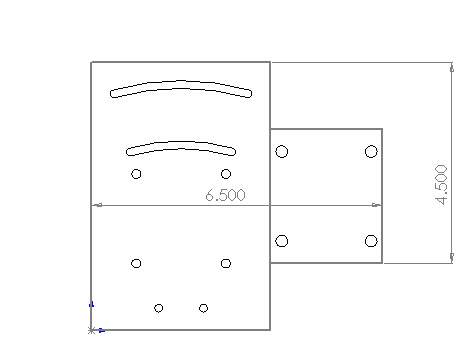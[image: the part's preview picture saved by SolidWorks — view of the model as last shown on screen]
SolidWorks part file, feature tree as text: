
SOLIDWORKS PART (.sldprt)
format: sldprt  version: not decoded by parser v0  size: 266,240 bytes
history: native  units: mm
features: sketch x3, cut_extrude x2, material x1, extrude x1, pattern_linear x1 + 1 further entry (+12 scaffold rows collapsed)
feature tree (21):
  "Annotations"  RD1=165.1mm RD2=114.3mm
  scaffold x12  (default folders/planes/origin — collapsed)
  material  "Material <not specified>"
  sketch  "Sketch1"  dims[c1.D1=152.4mm c1.D2=101.6mm c1.D3=63.5mm c1.D4=63.5mm c2.D3=76.2mm c2.D4=63.5mm c2.D5=38.1mm]
  extrude  "Extrude1"  Depth=12.7mm
  sketch  "Sketch4"  dims[c1.D3=6.6294mm c1.D6=4.3688mm c1.D9=~4.705401mm c1.D10=4.3688mm c2.D6=5.1054mm c2.D1=12.7mm c2.D2=6.35mm c2.D4=63.5mm c2.D5=6.35mm c2.D7=139.7mm c2.D8=25.4mm c2.D9=25.4mm c2.D11=105.41mm c3.D4=88.9mm c3.D5=25.4mm]
  cut_extrude  "Cut-Extrude2"  Depth=12.7mm
  pattern_linear  "LPattern2"  Count1=2 Count2=2 Spacing1=50.8mm Spacing2=50.8mm
  sketch  "Sketch5"  dims[c1.D6=105.41mm c1.D13=4.3942mm c1.D16=4.3942mm c1.D1=3.81mm c1.D2=50.8mm c1.D3=12.7mm c1.D4=139.7mm c1.D5=139.7mm c2.D6=25.4mm c2.D5=12.7mm c2.D11=12.7mm c2.D12=25.4mm c2.D13=12.7mm c2.D18=6.35mm c2.D19=12.7mm c2.D20=12.7mm c2.D2=50.8mm c3.D11=12.7mm c3.D12=12.7mm c3.D14=12.7mm c3.D15=12.7mm c3.D7=2.1844mm c3.D8=2.1844mm c3.D9=2.1844mm c3.D10=2.1844mm c4.D14=2.1844mm c4.D15=2.1844mm c4.D16=2.1844mm c4.D17=2.1844mm c4.D7=2.1844mm c4.D8=2.1844mm c4.D9=2.1844mm c4.D10=2.1844mm]
  cut_extrude  "Cut-Extrude4"  [1 undecoded]
decode coverage: 6 of 7 modeling features carry decoded parameters; 1 rows unclassified (native names shown)
note: ~ marks probable driven/reference dimensions
note: 1 parameter value undecoded
note: suppression state not decoded; provenance and decode notes live in map.json
